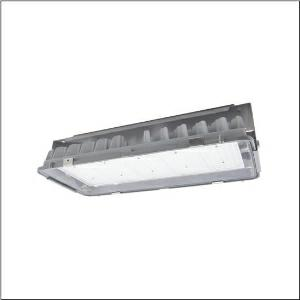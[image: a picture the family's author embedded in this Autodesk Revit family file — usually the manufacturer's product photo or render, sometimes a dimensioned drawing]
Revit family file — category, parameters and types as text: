
# Revit family: highbay_11xtreme_51hf81da4nma
name_source: partatom
category: Lighting Fixtures
units: mm (PartAtom-declared; Revit-internal decimal feet)

## family parameters
Cut with Voids When Loaded = No
Host = Face
Light Source = No
Part Type = Normal
Room Calculation Point = No
Round Connector Dimension = Use Diameter
Shared = No

## types (1)
- --- (1 x LED, 34200 lm, 188.1 W, 4000K)
    Apparent Load = 188 VA
    CIE Flux Codes = 88 96 99 100 100
    Color Rendering = 80
    Color Temperature = 4000K
    Default Elevation = 1800 mm
    Description = Highbay 11Xtreme, high bay luminaire, primary light control with lens, of PMMA, primary optical cover: cover, of toughened safety glass, light emission: direct distribution, primary light characteristic: symmetric, installation type: suspended mounting, surface-mounted, 1x LED module,for 1x LED, rated luminous flux: 34.200lm, luminous efficacy: 182lm/W, light colour: 840, colour temperature: 4000K, control gear: DALI 2, with cable H07RN-F 5x 1.5mm², mains connection: 220..240V, AC, 50/60Hz, cable length: 1,5m, rated input power: 188W, luminaire housing, of diecast aluminium, partly coated, silver, length: 595mm, width: 280mm, height: 195mm, protection rating (complete): IP66, insulation class (complete): insulation class I (protective earthing), certification: CE, ENEC, UKCA, protection symbol: D, ball protection: ball impact resistant according to DIN VDE 0710 part 13 (with chain suspension), impact resistance: IK08, permissible operating ambient temperature: -25..+45°C, reducing of maximum allowable ambient temperature of 5°C with ceiling mounting, packaging unit: 1 piece
    Height = 157 mm
    Lamp = 1 x LED
    Lamp Light Flux = 34200 lm
    Lamp Power = 188.1 W
    Lamp count = 1
    Length = 593 mm
    Luminous efficacy = 182 lm/W
    Manufacturer = Siteco
    ModVariant = No
    Model = 51HF81DA4NMA
    Mounting Place = Ceiling
    Mounting Type = Pendant
    Number of Poles = 1
    OnlyDefault = Yes
    Power Factor = 1
    Product Name = Highbay 11Xtreme
    Product group = high bay luminaire
    ProductGroupID = 901
    Protection Class = Protection class I
    Protection Degree = IP 66
    RLX_Detail_Level = 1
    RLX_Emergency_Light_Flux = 0 lm
    RLX_Emergency_Type = 0
    RLX_Emergency_Type_DB = No
    RlxData = <blob elided: 27861 chars, md5=9fc9a495>
    Socket = socket
    Standby Power = 0 W
    System Light Flux = 34200 lm
    System Power = 188 W
    Type Comments = factory setting: luminous flux: 100 % | dim-lin: 254 | 1258 mA
    Type Image = l_1258342.jpg
    URL = http://relux.com
    VarID = @adj_083656
    Voltage = 0 V
    Weight = 0.00 kg
    Width = 278 mm

## geometry (parser evidence)
native form markers: Blend x4, Sweep x10
no freeform markers — native parametric forms only
